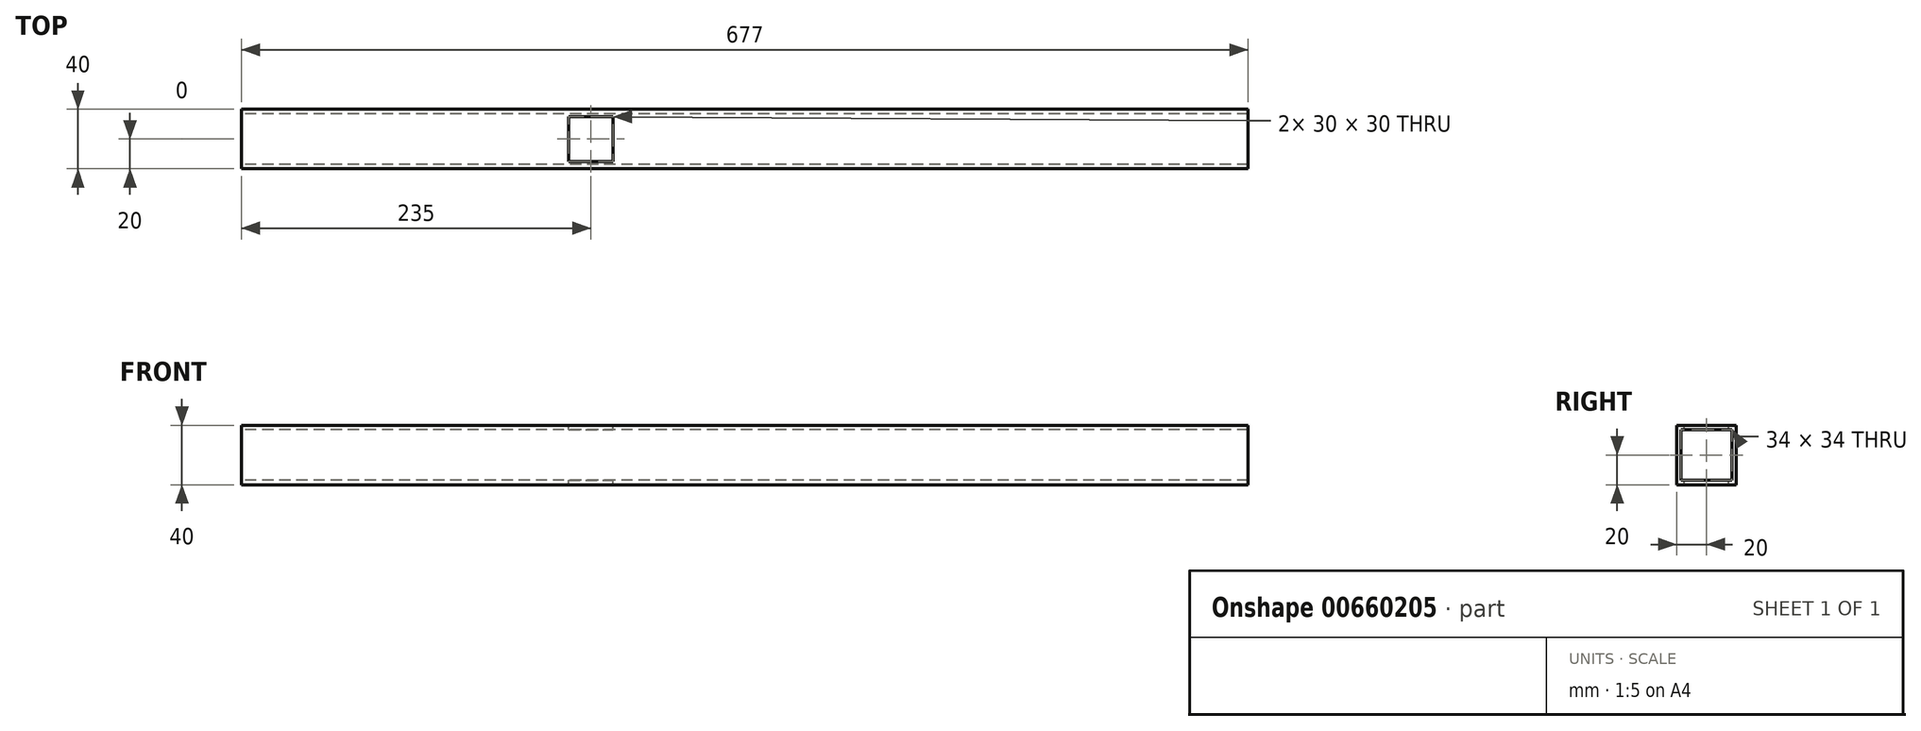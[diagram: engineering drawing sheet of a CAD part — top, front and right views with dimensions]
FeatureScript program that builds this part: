
annotation { "Feature Type Name" : "Feature", "Feature Type Description" : "" }
export const myFeature = defineFeature(function(context is Context, id is Id, definition is map)
    precondition{}
    {
        {
            var Q0;
            Q0=qCreatedBy(makeId("Right.planeOp"),FACE);
            var sketch = newSketch(context, id + "F0", { "sketchPlane" : qUnion([Q0])});
            skLineSegment(sketch, "E0.bottom", {"start": v(-20, 20) * mm, "end": v(20, 20) * mm});
            skLineSegment(sketch, "E0.top", {"start": v(-20, -20) * mm, "end": v(20, -20) * mm});
            skLineSegment(sketch, "E0.left", {"start": v(-20, 20) * mm, "end": v(-20, -20) * mm});
            skLineSegment(sketch, "E0.right", {"start": v(20, 20) * mm, "end": v(20, -20) * mm});
            skLineSegment(sketch, "E1.bottom", {"start": v(-17, 17) * mm, "end": v(17, 17) * mm});
            skLineSegment(sketch, "E1.top", {"start": v(-17, -17) * mm, "end": v(17, -17) * mm});
            skLineSegment(sketch, "E1.left", {"start": v(-17, 17) * mm, "end": v(-17, -17) * mm});
            skLineSegment(sketch, "E1.right", {"start": v(17, 17) * mm, "end": v(17, -17) * mm});
            skSolve(sketch);
        }
        {
            var Q0;
            Q0=makeQuery(id+"F0.imprint","IMPRINT",FACE,{"disambiguationData":[TD([[makeQuery(id+"F0.imprint","IMPRINT",EDGE,{"derivedFrom":sQuery(id+"F0.wireOp",EDGE,"E0.bottom")}),-1.0]])]});
            extrude(context, id + "F1", {"entities" : qUnion([Q0]), "endBound" : BoundingType.SYMMETRIC, "depth" : 677 * mm, "offsetDistance" : 25 * mm});
        }
        {
            var Q0;
            Q0=makeQuery(id+"F1.opExtrude","SWEPT_FACE",FACE,{"disambiguationData":[OSD([sQuery(id+"F0.wireOp",EDGE,"E0.bottom")])]});
            var sketch = newSketch(context, id + "F2", { "sketchPlane" : qUnion([Q0])});
            skLineSegment(sketch, "E2.bottom", {"start": v(-118.5, 15) * mm, "end": v(-88.5, 15) * mm});
            skLineSegment(sketch, "E2.top", {"start": v(-118.5, -15) * mm, "end": v(-88.5, -15) * mm});
            skLineSegment(sketch, "E2.left", {"start": v(-118.5, 15) * mm, "end": v(-118.5, -15) * mm});
            skLineSegment(sketch, "E2.right", {"start": v(-88.5, 15) * mm, "end": v(-88.5, -15) * mm});
            skSolve(sketch);
        }
        {
            var Q0;
            Q0 = qSketchRegion(id + "F2", true);
            extrude(context, id + "F3", {"entities" : qUnion([Q0]), "operationType" : NewBodyOperationType.REMOVE, "endBound" : BoundingType.THROUGH_ALL, "oppositeDirection" : true, "depth" : 25 * mm, "offsetDistance" : 25 * mm});
        }
    });
